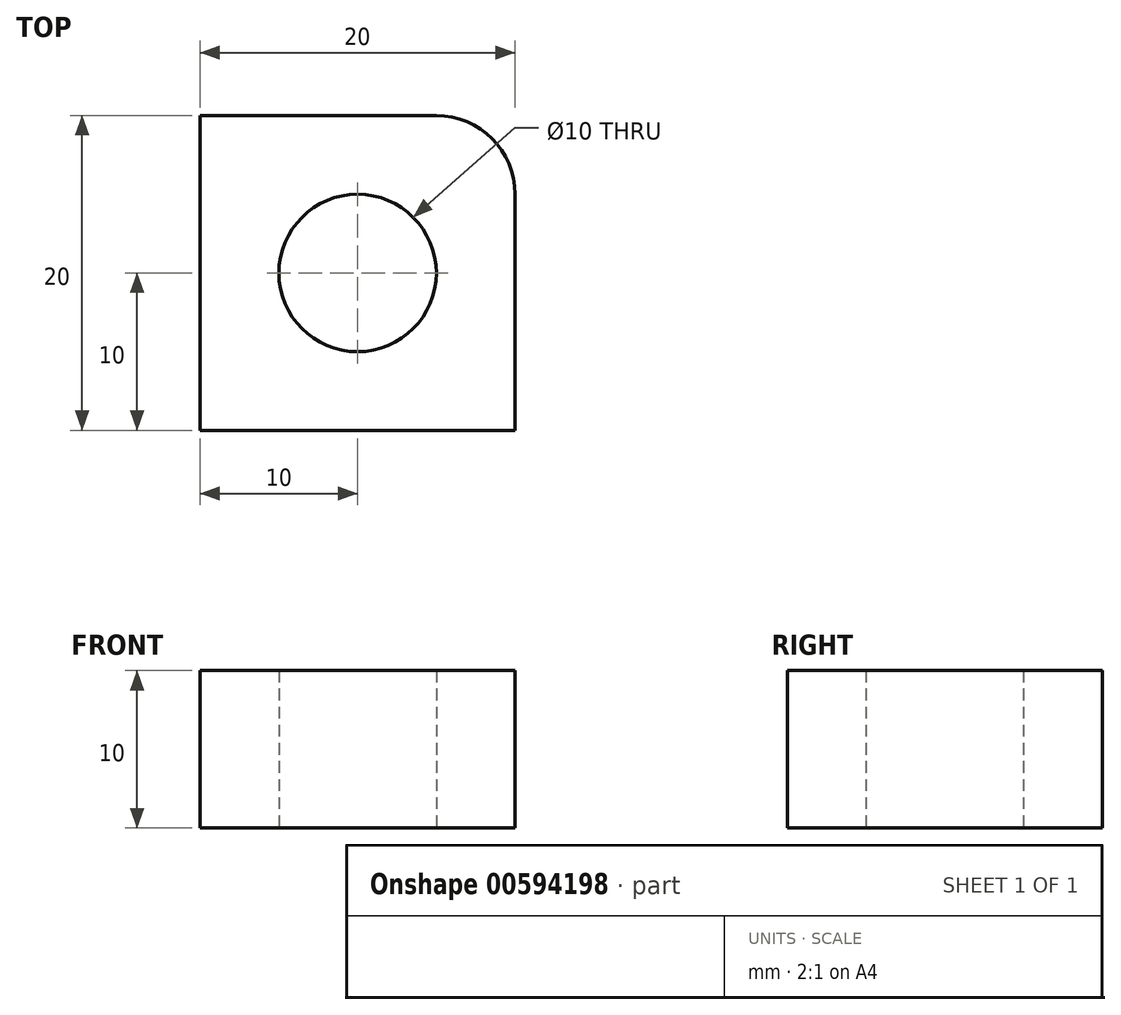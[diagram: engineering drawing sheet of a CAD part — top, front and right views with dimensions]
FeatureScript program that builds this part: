
annotation { "Feature Type Name" : "Feature", "Feature Type Description" : "" }
export const myFeature = defineFeature(function(context is Context, id is Id, definition is map)
    precondition{}
    {
        {
            var Q0;
            Q0=qCreatedBy(makeId("Top.planeOp"),FACE);
            var sketch = newSketch(context, id + "F0", { "sketchPlane" : qUnion([Q0])});
            skLineSegment(sketch, "E0.bottom", {"start": v(10, -10) * mm, "end": v(-10, -10) * mm});
            skLineSegment(sketch, "E0.top", {"start": v(5, 10) * mm, "end": v(-10, 10) * mm});
            skLineSegment(sketch, "E0.left", {"start": v(10, -10) * mm, "end": v(10, 5) * mm});
            skLineSegment(sketch, "E0.right", {"start": v(-10, -10) * mm, "end": v(-10, 10) * mm});
            skPoint(sketch, "E0.middle", {"position": v(0, 0) * mm});
            skCircle(sketch, "E1", {"center": v(0, 0) * mm, "radius": 5 * mm});
            skPoint(sketch, "E2.visualSharp", {"position": v(10, 10) * mm});
            skArc(sketch, "E2.filletArc", {"start": v(10, 5) * mm, "mid": v(8.54, 8.54) * mm, "end": v(5, 10) * mm});
            skSolve(sketch);
        }
        {
            var Q0;
            Q0=makeQuery(id+"F0.imprint","IMPRINT",FACE,{"disambiguationData":[TD([[makeQuery(id+"F0.imprint","IMPRINT",EDGE,{"derivedFrom":sQuery(id+"F0.wireOp",EDGE,"E0.bottom")}),-1.0]])]});
            extrude(context, id + "F1", {"entities" : qUnion([Q0]), "depth" : 10 * mm, "offsetDistance" : 25 * mm});
        }
    });
